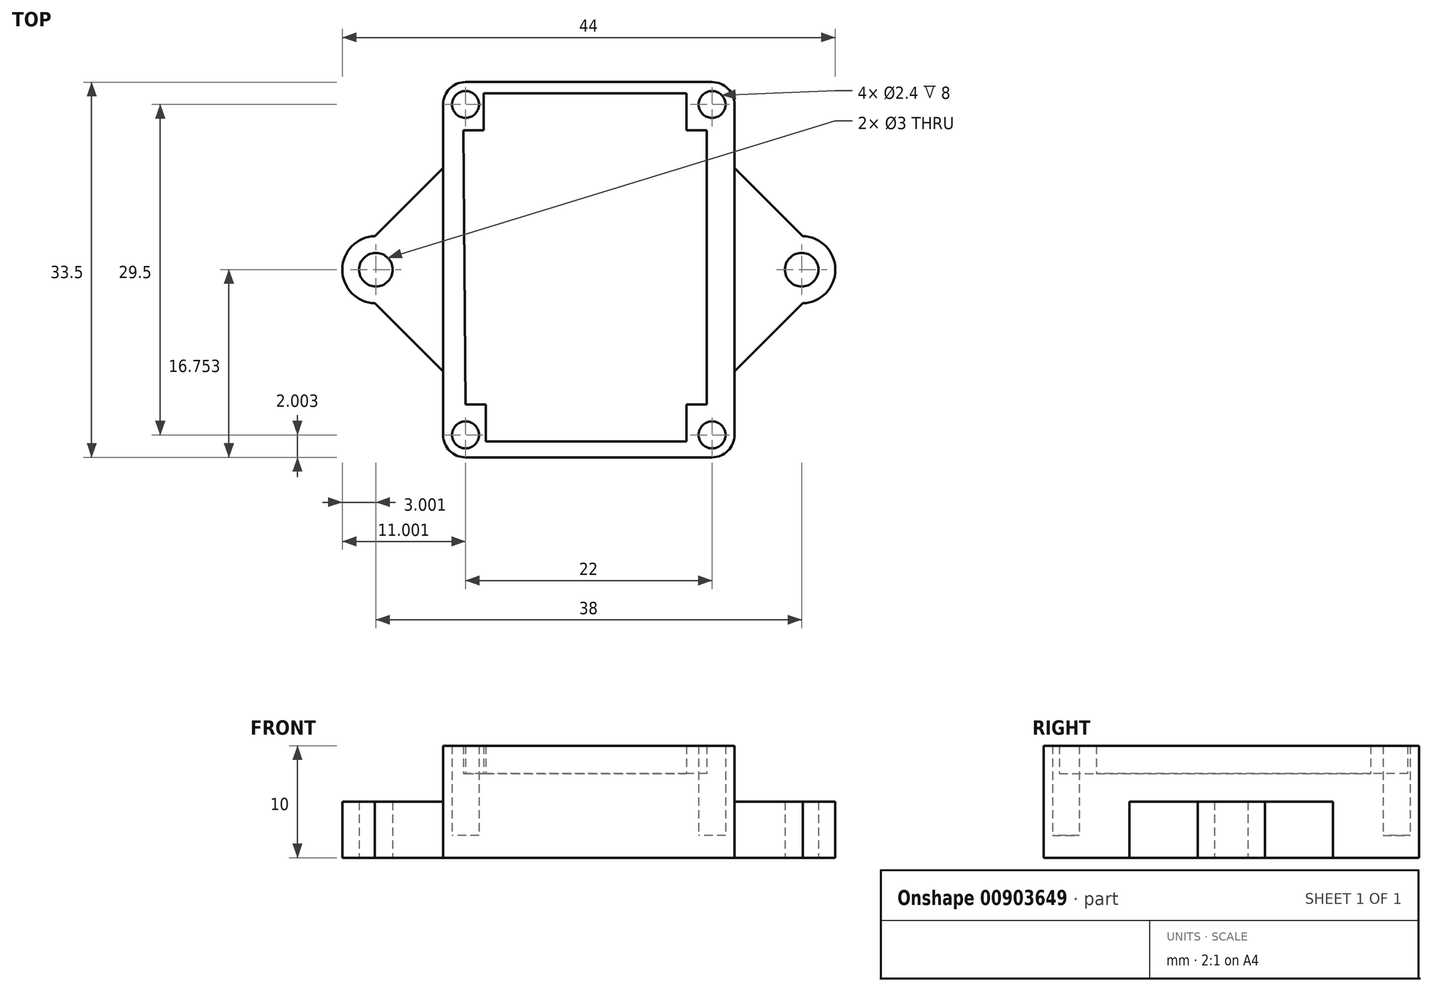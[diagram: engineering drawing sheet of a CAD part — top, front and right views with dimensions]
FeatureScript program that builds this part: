
annotation { "Feature Type Name" : "Feature", "Feature Type Description" : "" }
export const myFeature = defineFeature(function(context is Context, id is Id, definition is map)
    precondition{}
    {
        {
            var Q0;
            Q0=qCreatedBy(makeId("Top.planeOp"),FACE);
            var sketch = newSketch(context, id + "F0", { "sketchPlane" : qUnion([Q0])});
            skLineSegment(sketch, "E0.bottom", {"start": v(-10.15, 11.5) * mm, "end": v(11.85, 11.5) * mm});
            skLineSegment(sketch, "E0.top", {"start": v(-10.15, -22) * mm, "end": v(11.85, -22) * mm});
            skLineSegment(sketch, "E0.left", {"start": v(-12.15, 9.5) * mm, "end": v(-12.15, -20) * mm});
            skLineSegment(sketch, "E0.right", {"start": v(13.85, 9.5) * mm, "end": v(13.85, -20) * mm});
            skPoint(sketch, "E1.visualSharp", {"position": v(-12.15, 11.5) * mm});
            skArc(sketch, "E1.filletArc", {"start": v(-10.15, 11.5) * mm, "mid": v(-11.56, 10.92) * mm, "end": v(-12.15, 9.5) * mm});
            skPoint(sketch, "E2.visualSharp", {"position": v(13.85, 11.5) * mm});
            skArc(sketch, "E2.filletArc", {"start": v(13.85, 9.5) * mm, "mid": v(13.27, 10.92) * mm, "end": v(11.85, 11.5) * mm});
            skPoint(sketch, "E3.visualSharp", {"position": v(13.85, -22) * mm});
            skArc(sketch, "E3.filletArc", {"start": v(11.85, -22) * mm, "mid": v(13.27, -21.41) * mm, "end": v(13.85, -20) * mm});
            skPoint(sketch, "E4.visualSharp", {"position": v(-12.15, -22) * mm});
            skArc(sketch, "E4.filletArc", {"start": v(-12.15, -20) * mm, "mid": v(-11.56, -21.41) * mm, "end": v(-10.15, -22) * mm});
            skCircle(sketch, "E5", {"center": v(-10.15, 9.5) * mm, "radius": 1.2 * mm});
            skCircle(sketch, "E6", {"center": v(11.85, -20) * mm, "radius": 1.2 * mm});
            skCircle(sketch, "E7", {"center": v(-10.15, -20) * mm, "radius": 1.2 * mm});
            skCircle(sketch, "E8", {"center": v(11.85, 9.5) * mm, "radius": 1.2 * mm});
            skLineSegment(sketch, "E9", {"start": v(-8.53, 10.5) * mm, "end": v(-8.53, 7.2) * mm});
            skLineSegment(sketch, "E10", {"start": v(-8.53, 7.2) * mm, "end": v(-10.35, 7.2) * mm});
            skLineSegment(sketch, "E11", {"start": v(-10.35, 7.2) * mm, "end": v(-10.15, -17.3) * mm});
            skLineSegment(sketch, "E12", {"start": v(-10.15, -17.3) * mm, "end": v(-8.32, -17.28) * mm});
            skLineSegment(sketch, "E13", {"start": v(-8.32, -17.28) * mm, "end": v(-8.32, -20.59) * mm});
            skLineSegment(sketch, "E14", {"start": v(-8.32, -20.59) * mm, "end": v(9.56, -20.59) * mm});
            skLineSegment(sketch, "E15", {"start": v(9.56, -20.59) * mm, "end": v(9.56, -17.28) * mm});
            skLineSegment(sketch, "E16", {"start": v(9.56, -17.28) * mm, "end": v(11.38, -17.28) * mm});
            skLineSegment(sketch, "E17", {"start": v(11.38, -17.28) * mm, "end": v(11.38, 7.2) * mm});
            skLineSegment(sketch, "E18", {"start": v(11.38, 7.2) * mm, "end": v(9.56, 7.2) * mm});
            skLineSegment(sketch, "E19", {"start": v(9.56, 7.2) * mm, "end": v(9.56, 10.5) * mm});
            skLineSegment(sketch, "E20", {"start": v(9.56, 10.5) * mm, "end": v(-8.53, 10.5) * mm});
            skLineSegment(sketch, "E21", {"start": v(-12.15, -5.25) * mm, "end": v(-18.15, -5.25) * mm, "construction": true});
            skArc(sketch, "E22", {"start": v(-18.24, -2.25) * mm, "mid": v(-21.15, -5.28) * mm, "end": v(-18.17, -8.25) * mm});
            skLineSegment(sketch, "E23", {"start": v(-18.24, -2.25) * mm, "end": v(-12.15, 3.84) * mm});
            skLineSegment(sketch, "E24.MirrorCS", {"start": v(-18.24, -8.25) * mm, "end": v(-12.15, -14.33) * mm});
            skCircle(sketch, "E25", {"center": v(-18.15, -5.25) * mm, "radius": 1.5 * mm});
            skLineSegment(sketch, "E26", {"start": v(0.85, 11.5) * mm, "end": v(0.85, -22) * mm, "construction": true});
            skLineSegment(sketch, "E27.MirrorCS", {"start": v(19.94, -8.25) * mm, "end": v(13.85, -14.33) * mm});
            skArc(sketch, "E28.MirrorCS", {"start": v(19.94, -2.25) * mm, "mid": v(22.85, -5.28) * mm, "end": v(19.88, -8.25) * mm});
            skCircle(sketch, "E29.MirrorC", {"center": v(19.85, -5.25) * mm, "radius": 1.5 * mm});
            skLineSegment(sketch, "E30.MirrorCS", {"start": v(19.94, -2.25) * mm, "end": v(13.85, 3.84) * mm});
            skLineSegment(sketch, "E31.MirrorCS", {"start": v(13.85, -5.25) * mm, "end": v(19.85, -5.25) * mm, "construction": true});
            skSolve(sketch);
        }
        {
            var Q0;
            {var subQ1=sQuery(id+"F0.wireOp",EDGE,"E23");Q0=makeQuery(id+"F0.imprint","IMPRINT",FACE,{"disambiguationData":[TD([[makeQuery(id+"F0.imprint","IMPRINT",EDGE,{"derivedFrom":subQ1}),-1.0]])]});}
            var Q1;
            {var subQ1=sQuery(id+"F0.wireOp",EDGE,"E27.MirrorCS");Q1=makeQuery(id+"F0.imprint","IMPRINT",FACE,{"disambiguationData":[TD([[makeQuery(id+"F0.imprint","IMPRINT",EDGE,{"derivedFrom":subQ1}),-1.0]])]});}
            extrude(context, id + "F1", {"entities" : qUnion([Q0, Q1]), "depth" : 5 * mm, "offsetDistance" : 25 * mm});
        }
        {
            var Q0;
            Q0=makeQuery(id+"F0.imprint","IMPRINT",FACE,{"disambiguationData":[TD([[makeQuery(id+"F0.imprint","IMPRINT",EDGE,{"derivedFrom":sQuery(id+"F0.wireOp",EDGE,"E0.bottom")}),-1.0]])]});
            extrude(context, id + "F2", {"entities" : qUnion([Q0]), "depth" : 10 * mm, "offsetDistance" : 25 * mm});
        }
        {
            var Q0;
            Q0=makeQuery(id+"F0.imprint","IMPRINT",FACE,{"disambiguationData":[TD([[makeQuery(id+"F0.imprint","IMPRINT",EDGE,{"derivedFrom":sQuery(id+"F0.wireOp",EDGE,"E9")}),1.0]])]});
            extrude(context, id + "F3", {"entities" : qUnion([Q0]), "operationType" : NewBodyOperationType.ADD, "depth" : 7.5 * mm, "offsetDistance" : 25 * mm});
        }
        {
            var Q0;
            Q0=makeQuery(id+"F0.imprint","IMPRINT",FACE,{"disambiguationData":[TD([[makeQuery(id+"F0.imprint","IMPRINT",EDGE,{"derivedFrom":sQuery(id+"F0.wireOp",EDGE,"E5")}),1.0]])]});
            var Q1;
            Q1=makeQuery(id+"F0.imprint","IMPRINT",FACE,{"disambiguationData":[TD([[makeQuery(id+"F0.imprint","IMPRINT",EDGE,{"derivedFrom":sQuery(id+"F0.wireOp",EDGE,"E8")}),1.0]])]});
            var Q2;
            Q2=makeQuery(id+"F0.imprint","IMPRINT",FACE,{"disambiguationData":[TD([[makeQuery(id+"F0.imprint","IMPRINT",EDGE,{"derivedFrom":sQuery(id+"F0.wireOp",EDGE,"E6")}),1.0]])]});
            var Q3;
            Q3=makeQuery(id+"F0.imprint","IMPRINT",FACE,{"disambiguationData":[TD([[makeQuery(id+"F0.imprint","IMPRINT",EDGE,{"derivedFrom":sQuery(id+"F0.wireOp",EDGE,"E7")}),1.0]])]});
            extrude(context, id + "F4", {"entities" : qUnion([Q0, Q1, Q2, Q3]), "operationType" : NewBodyOperationType.ADD, "depth" : 2 * mm, "offsetDistance" : 25 * mm});
        }
    });
